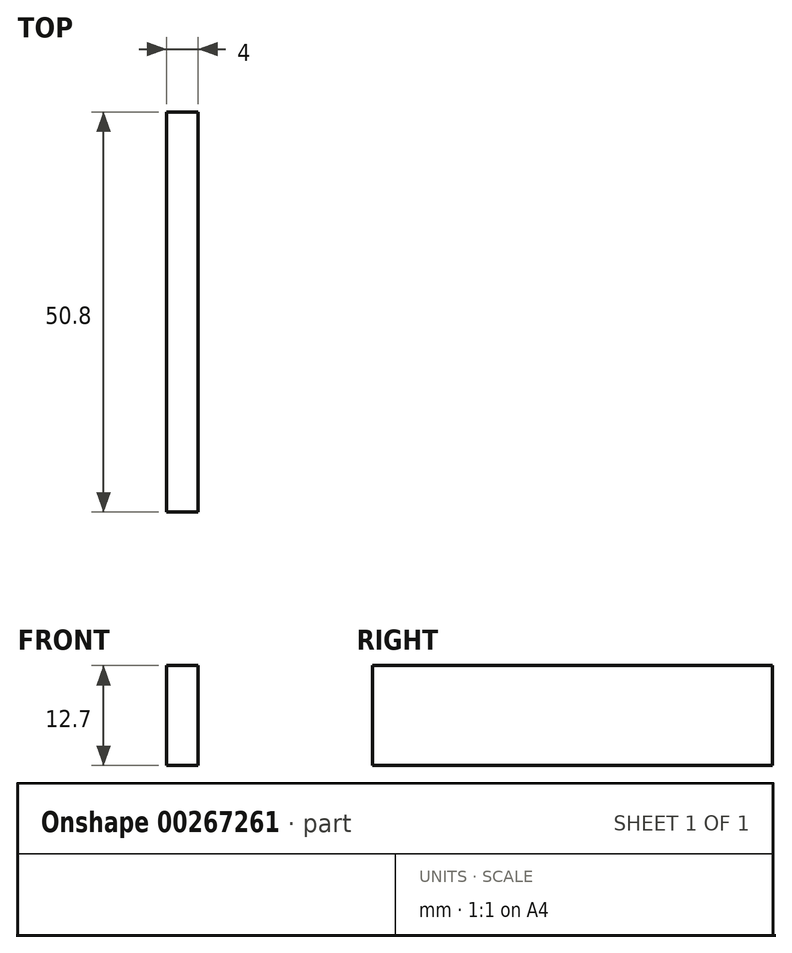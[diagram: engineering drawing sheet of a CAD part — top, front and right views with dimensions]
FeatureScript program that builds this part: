
annotation { "Feature Type Name" : "Feature", "Feature Type Description" : "" }
export const myFeature = defineFeature(function(context is Context, id is Id, definition is map)
    precondition{}
    {
        {
            assignVariable(context, id + "F0", {"name" : "DockWidth", "anyValue" : 4});
        }
        {
            var Q0;
            Q0=qCreatedBy(makeId("Right.planeOp"),FACE);
            var sketch = newSketch(context, id + "F1", { "sketchPlane" : qUnion([Q0])});
            skLineSegment(sketch, "E0.bottom", {"start": v(0, 0) * mm, "end": v(50.8, 0) * mm});
            skLineSegment(sketch, "E0.top", {"start": v(0, -12.7) * mm, "end": v(50.8, -12.7) * mm});
            skLineSegment(sketch, "E0.left", {"start": v(0, 0) * mm, "end": v(0, -12.7) * mm});
            skLineSegment(sketch, "E0.right", {"start": v(50.8, 0) * mm, "end": v(50.8, -12.7) * mm});
            skSolve(sketch);
        }
        {
            var Q0;
            Q0 = qSketchRegion(id + "F1", true);
            extrude(context, id + "F2", {"entities" : qUnion([Q0]), "oppositeDirection" : true, "depth" : (getVariable(context, 'DockWidth')) * mm});
        }
    });
